# Revit family: Clevertronics_LIFELIGHT PRO RECESSED EMERGENCY_CIRCLE
name_source: partatom
category: Lighting Fixtures
units: mm (PartAtom-declared; Revit-internal decimal feet)

## family parameters
Cut with Voids When Loaded = No
Host = Face
Light Source = Yes
Part Type = Normal
Room Calculation Point = No
Round Connector Dimension = Use Diameter
Shared = No

## types (8) — shared parameters
Clevertronics_AS2293 Classification = C0=D40 C90=D40
Clevertronics_Apparent Load = 3 VA
Clevertronics_Applicable Standards = AS/NZS3820, CISPR15, AS/NZS2293.3
Clevertronics_Battery = 3.2V 6400mAh
Clevertronics_Battery Type = Lithium Iron Phosphate
Clevertronics_Charger Method = Intelligent current limited constant voltage
Clevertronics_Construction = PC/ABS head
Clevertronics_Depth = 4 mm  [stored 0.0131234 ft]
Clevertronics_Dimensions LED Enclosure = 60mm head diameter (95mm with adaptor plate)
Clevertronics_Dimensions Main Enclosure = 232mm x 40mm x 40mm (Control pack)
Clevertronics_IP Rating = IP20
Clevertronics_Mounting = Recessed mount
Clevertronics_Operating Mode = Non-maintained
Clevertronics_Operating Temperature = 1˚C to 40˚C
Clevertronics_Operating Voltage = 240V AC; 50Hz
Clevertronics_Power Consumption = 0.7 Watts (Standby), 3.0 Watts (Max)
Clevertronics_Product Description = LP Premium Lifelight, High Performance, Recessed Emergency Light
LP Premium Lifelight, High Performance, Recessed Emergency Light
with 4 Hour Emergency Operation
Clevertronics_Replacement Battery = 1550230 BATT:LP 3.2V 6400mAh.200mm lead.Brkt
Clevertronics_Replacement Driver = CLIFE-PRO-CKIT-335
Clevertronics_Replacement Lamp = 8003081 LED: PCA: LLPRO HEAD Alum #CT10640-D4 - GW CSHPM 'LT'
Clevertronics_Weight = 0.8kg
Clevertronics_Width Adaptor = 95 mm
Color Filter = 16777215
Default Elevation = 1219 mm
Dimming Lamp Color Temperature Shift = <None>
Emit Shape Visible in Rendering = No
Emit from Circle Diameter = 610 mm
Lamp = Dual LED (Lifetime warranty on the lamp head and loom assembly)
Manufacture_ANZRS = Clevertronics
Manufacturer = Clevertronics
Photometric Web File = CLIFE-PRO _IESA_E_LL22009B_20190729.IES
Tilt Angle = -90.00°
URL = https://clevertronics.com.au
calc_adaptor radius = 48 mm  [stored 0.15748 ft]

## per-type parameters (varying)
| type | Clevertronics_MIC Number | Clevertronics_Material | Clevertronics_Testing Node | Clevertronics_Testing System | Description |
| CLIFE-HV-4HR-BLK | AUD02810210001 | Clevertronics_Plastic_Black | 8003191 | Zoneworks XT HIVE (RF) | LP Premium Lifelight, High Performance, Recessed Emergency Light
with 4 Hour Emergency Operation, Black |
| CLIFE-HV-4HR | AUD02810170001 | Clevertronics_Plastic_White | 8003191 | Zoneworks XT HIVE (RF) | LP Premium Lifelight, High Performance, Recessed Emergency Light
with 4 Hour Emergency Operation |
| CLIFE-DALI-4HR |  | Clevertronics_Plastic_White |  | DALI |  |
| CLIFE-4HR |  | Clevertronics_Plastic_White |  | CTP |  |
| CLIFE-ZW-4HR |  | Clevertronics_Plastic_White |  | Zoneworks Powerline |  |
| CLIFE-DALI-4HR-BLK |  | Clevertronics_Plastic_Black |  | DALI |  |
| CLIFE-4HR-BLK |  | Clevertronics_Plastic_Black |  | CTP |  |
| CLIFE-ZW-4HR-BLK |  | Clevertronics_Plastic_Black |  | Zoneworks Powerline |  |

note: column(s) folded — value = type name in every type: Model

note: [stored X ft] marks values corroborated as IEEE doubles in the binary element streams (Revit-internal decimal feet)

## geometry (parser evidence)
native form markers: Sweep x4
no freeform markers — native parametric forms only
